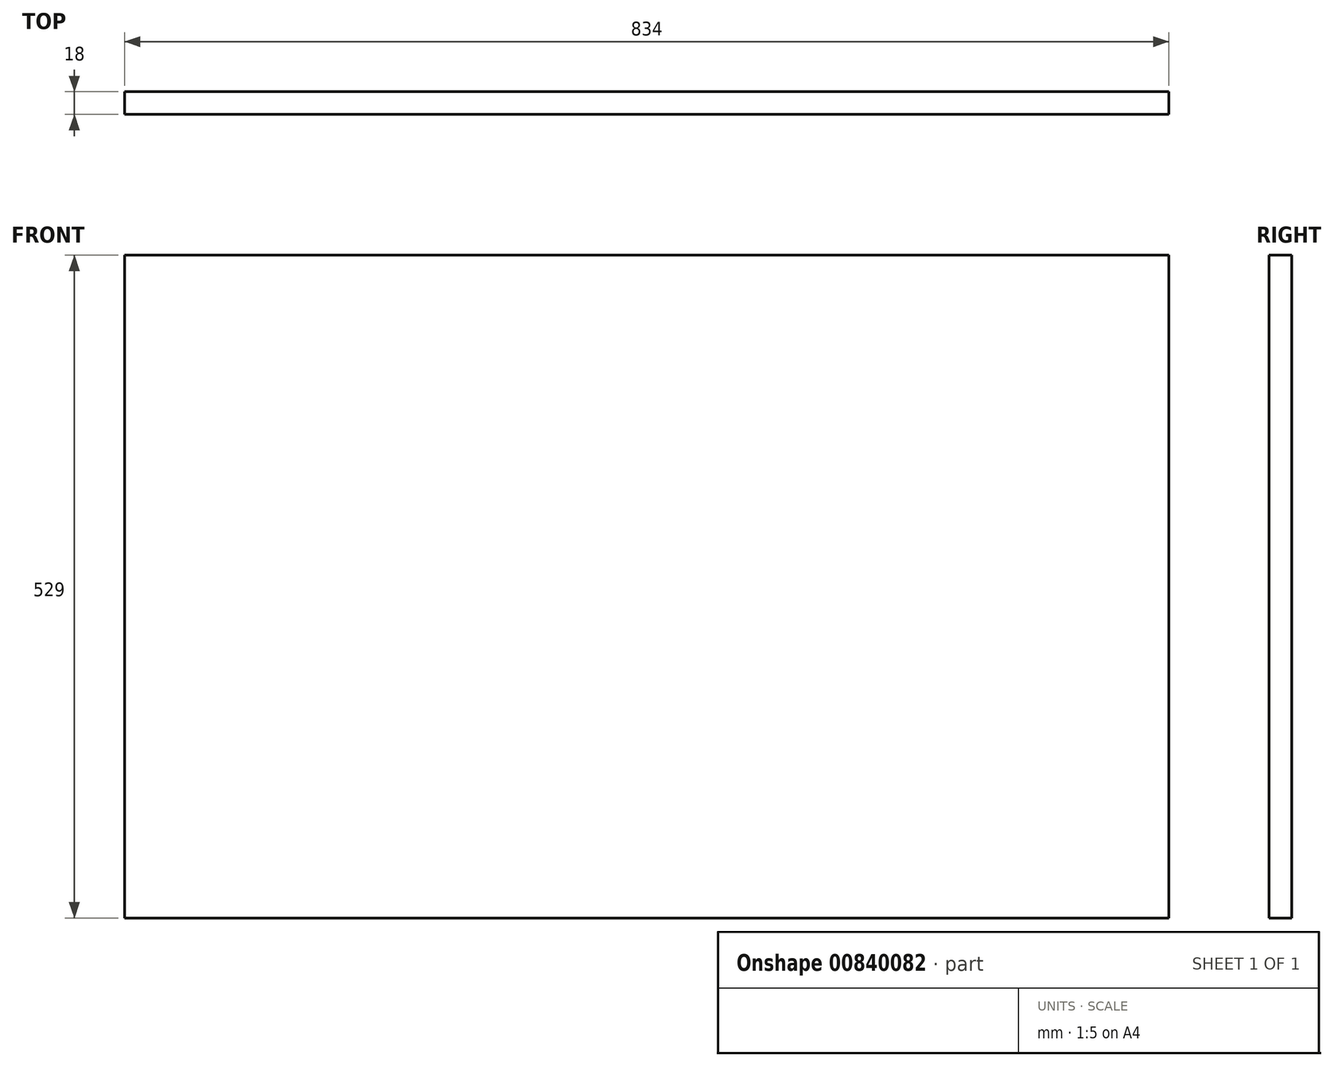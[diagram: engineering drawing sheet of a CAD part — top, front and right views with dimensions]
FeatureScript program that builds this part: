
annotation { "Feature Type Name" : "Feature", "Feature Type Description" : "" }
export const myFeature = defineFeature(function(context is Context, id is Id, definition is map)
    precondition{}
    {
        {
            var Q0;
            Q0=qCreatedBy(makeId("Front.planeOp"),FACE);
            var sketch = newSketch(context, id + "F0", { "sketchPlane" : qUnion([Q0])});
            skLineSegment(sketch, "E0.bottom", {"start": v(-417, 264.5) * mm, "end": v(417, 264.5) * mm});
            skLineSegment(sketch, "E0.top", {"start": v(-417, -264.5) * mm, "end": v(417, -264.5) * mm});
            skLineSegment(sketch, "E0.left", {"start": v(-417, 264.5) * mm, "end": v(-417, -264.5) * mm});
            skLineSegment(sketch, "E0.right", {"start": v(417, 264.5) * mm, "end": v(417, -264.5) * mm});
            skLineSegment(sketch, "E1", {"start": v(-417, 264.5) * mm, "end": v(417, -264.5) * mm, "construction": true});
            skSolve(sketch);
        }
        {
            var Q0;
            Q0=qSketchRegion(id+"F0",true);
            extrude(context, id + "F1", {"entities" : qUnion([Q0]), "depth" : 18 * mm, "offsetDistance" : 25 * mm});
        }
    });
